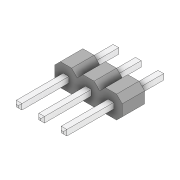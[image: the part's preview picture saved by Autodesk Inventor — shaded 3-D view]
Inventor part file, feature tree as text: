
AUTODESK INVENTOR PART (.ipt)
format: ipt  version: 2022 (Build 260153000, 153)  size: 126,976 bytes
history: imported  units: in
note: dims shown in document units (in); Inventor stores cm internally (conversion verified against a paired STEP export)
features: imported_body x1
ambient origin geometry x8: Origin, YZ Plane, XZ Plane, XY Plane, X Axis, Y Axis, Z Axis, Center Point
bodies: Solid1 (imported_parasolid), Body1 (imported_parasolid)
feature tree (1):
  imported_body  NMx_Import_Brep_tag  [imported B-rep: ~76 faces, bbox_mm=[7.62, 2.54, 11.34]]
